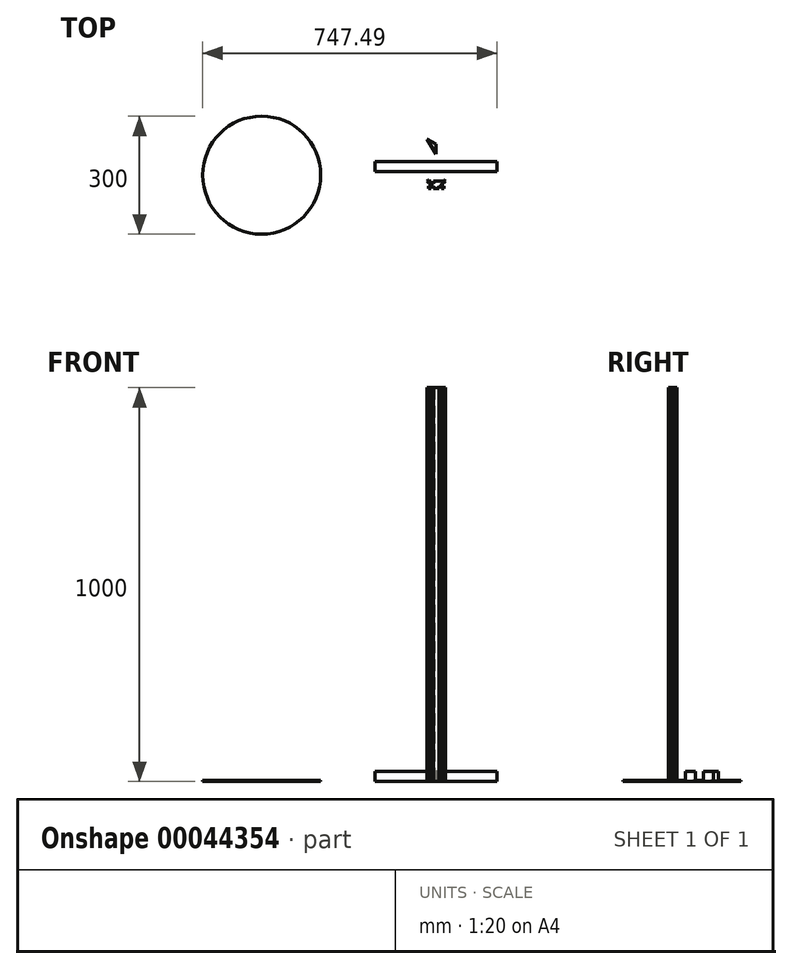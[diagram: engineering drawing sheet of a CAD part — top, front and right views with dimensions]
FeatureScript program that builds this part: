
annotation { "Feature Type Name" : "Feature", "Feature Type Description" : "" }
export const myFeature = defineFeature(function(context is Context, id is Id, definition is map)
    precondition{}
    {
        {
            var Q0;
            Q0=qCreatedBy(makeId("Top.planeOp"),FACE);
            var sketch = newSketch(context, id + "F0", { "sketchPlane" : qUnion([Q0])});
            skCircle(sketch, "E0", {"center": v(-442.49, 24.21) * mm, "radius": 150 * mm});
            skSolve(sketch);
        }
        {
            var Q0;
            Q0=qSketchRegion(id+"F0",true);
            extrude(context, id + "F1", {"entities" : qUnion([Q0]), "depth" : 3 * mm});
        }
        {
            var Q0;
            Q0=qCreatedBy(makeId("Top.planeOp"),FACE);
            var sketch = newSketch(context, id + "F2", { "sketchPlane" : qUnion([Q0])});
            skLineSegment(sketch, "E1", {"start": v(-19.2, 12.03) * mm, "end": v(-20, 12.03) * mm});
            skLineSegment(sketch, "E2", {"start": v(-20, 12.03) * mm, "end": v(-22.38, 9.65) * mm});
            skLineSegment(sketch, "E3", {"start": v(-22.38, 9.65) * mm, "end": v(-20, 7.28) * mm});
            skLineSegment(sketch, "E4", {"start": v(-20, 7.28) * mm, "end": v(-19.2, 7.28) * mm});
            skLineSegment(sketch, "E5", {"start": v(-19.2, 7.28) * mm, "end": v(-19.2, 2.65) * mm});
            skLineSegment(sketch, "E6", {"start": v(-19.2, 2.65) * mm, "end": v(-17.2, 2.65) * mm});
            skLineSegment(sketch, "E7", {"start": v(-17.2, 2.65) * mm, "end": v(-17.2, 5.65) * mm});
            skLineSegment(sketch, "E8", {"start": v(-17.2, 5.65) * mm, "end": v(-16.27, 5.65) * mm});
            skLineSegment(sketch, "E9", {"start": v(-16.27, 5.65) * mm, "end": v(-13.2, 2.6) * mm});
            skLineSegment(sketch, "E10", {"start": v(-13.2, 2.6) * mm, "end": v(-13.2, -3.29) * mm});
            skLineSegment(sketch, "E11", {"start": v(-13.2, -3.29) * mm, "end": v(-16.27, -6.35) * mm});
            skLineSegment(sketch, "E12", {"start": v(-16.27, -6.35) * mm, "end": v(-17.2, -6.35) * mm});
            skLineSegment(sketch, "E13", {"start": v(-17.2, -6.35) * mm, "end": v(-17.2, -3.35) * mm});
            skLineSegment(sketch, "E14", {"start": v(-17.2, -3.35) * mm, "end": v(-19.2, -3.35) * mm});
            skLineSegment(sketch, "E15", {"start": v(-19.2, -3.35) * mm, "end": v(-19.2, -10.35) * mm});
            skLineSegment(sketch, "E16", {"start": v(-19.2, -10.35) * mm, "end": v(-12.2, -10.35) * mm});
            skLineSegment(sketch, "E17", {"start": v(-12.2, -10.35) * mm, "end": v(-12.2, -8.35) * mm});
            skLineSegment(sketch, "E18", {"start": v(-12.2, -8.35) * mm, "end": v(-15.2, -8.35) * mm});
            skLineSegment(sketch, "E19", {"start": v(-15.2, -8.35) * mm, "end": v(-15.2, -7.4) * mm});
            skLineSegment(sketch, "E20", {"start": v(-15.2, -7.4) * mm, "end": v(-12.15, -4.35) * mm});
            skLineSegment(sketch, "E21", {"start": v(-12.15, -4.35) * mm, "end": v(-6.27, -4.35) * mm});
            skLineSegment(sketch, "E22", {"start": v(-6.27, -4.35) * mm, "end": v(-3.2, -7.4) * mm});
            skLineSegment(sketch, "E23", {"start": v(-3.2, -7.4) * mm, "end": v(-3.2, -8.35) * mm});
            skLineSegment(sketch, "E24", {"start": v(-3.2, -8.35) * mm, "end": v(-6.2, -8.35) * mm});
            skLineSegment(sketch, "E25", {"start": v(-6.2, -8.35) * mm, "end": v(-6.2, -10.35) * mm});
            skLineSegment(sketch, "E26", {"start": v(-6.2, -10.35) * mm, "end": v(7.8, -10.35) * mm});
            skLineSegment(sketch, "E27", {"start": v(7.8, -10.35) * mm, "end": v(7.8, -8.35) * mm});
            skLineSegment(sketch, "E28", {"start": v(7.8, -8.35) * mm, "end": v(4.8, -8.35) * mm});
            skLineSegment(sketch, "E29", {"start": v(4.8, -8.35) * mm, "end": v(4.8, -7.4) * mm});
            skLineSegment(sketch, "E30", {"start": v(4.8, -7.4) * mm, "end": v(7.85, -4.35) * mm});
            skLineSegment(sketch, "E31", {"start": v(7.85, -4.35) * mm, "end": v(13.73, -4.35) * mm});
            skLineSegment(sketch, "E32", {"start": v(13.73, -4.35) * mm, "end": v(16.8, -7.4) * mm});
            skLineSegment(sketch, "E33", {"start": v(16.8, -8.35) * mm, "end": v(13.8, -8.35) * mm});
            skLineSegment(sketch, "E34", {"start": v(13.8, -8.35) * mm, "end": v(13.8, -10.35) * mm});
            skLineSegment(sketch, "E35", {"start": v(13.8, -10.35) * mm, "end": v(20.8, -10.35) * mm});
            skLineSegment(sketch, "E36", {"start": v(20.8, -10.35) * mm, "end": v(20.8, -3.35) * mm});
            skLineSegment(sketch, "E37", {"start": v(20.8, -3.35) * mm, "end": v(18.8, -3.35) * mm});
            skLineSegment(sketch, "E38", {"start": v(18.8, -3.35) * mm, "end": v(18.8, -6.35) * mm});
            skLineSegment(sketch, "E39", {"start": v(18.8, -6.35) * mm, "end": v(17.85, -6.35) * mm});
            skLineSegment(sketch, "E40", {"start": v(17.85, -6.35) * mm, "end": v(14.8, -3.29) * mm});
            skLineSegment(sketch, "E41", {"start": v(14.8, -3.29) * mm, "end": v(14.8, 2.6) * mm});
            skLineSegment(sketch, "E42", {"start": v(14.8, 2.6) * mm, "end": v(17.85, 5.65) * mm});
            skLineSegment(sketch, "E43", {"start": v(17.85, 5.65) * mm, "end": v(18.8, 5.65) * mm});
            skLineSegment(sketch, "E44", {"start": v(18.8, 5.65) * mm, "end": v(18.8, 2.65) * mm});
            skLineSegment(sketch, "E45", {"start": v(18.8, 2.65) * mm, "end": v(20.8, 2.65) * mm});
            skLineSegment(sketch, "E46", {"start": v(20.8, 2.65) * mm, "end": v(20.8, 7.28) * mm});
            skLineSegment(sketch, "E47", {"start": v(23.97, 9.65) * mm, "end": v(21.6, 12.03) * mm});
            skLineSegment(sketch, "E48", {"start": v(21.6, 12.03) * mm, "end": v(20.8, 12.03) * mm});
            skLineSegment(sketch, "E49", {"start": v(20.8, 12.03) * mm, "end": v(20.8, 9.65) * mm});
            skLineSegment(sketch, "E50", {"start": v(20.8, 9.65) * mm, "end": v(-6.2, 9.65) * mm});
            skLineSegment(sketch, "E51", {"start": v(-6.2, 9.65) * mm, "end": v(-6.2, 7.65) * mm});
            skLineSegment(sketch, "E52", {"start": v(-6.2, 7.65) * mm, "end": v(-3.2, 7.65) * mm});
            skLineSegment(sketch, "E53", {"start": v(-3.2, 7.65) * mm, "end": v(-3.2, 6.71) * mm});
            skLineSegment(sketch, "E54", {"start": v(-3.2, 6.71) * mm, "end": v(-6.27, 3.65) * mm});
            skLineSegment(sketch, "E55", {"start": v(-6.27, 3.65) * mm, "end": v(-12.15, 3.65) * mm});
            skLineSegment(sketch, "E56", {"start": v(-12.15, 3.65) * mm, "end": v(-15.2, 6.71) * mm});
            skLineSegment(sketch, "E57", {"start": v(-15.2, 6.71) * mm, "end": v(-15.2, 7.65) * mm});
            skLineSegment(sketch, "E58", {"start": v(-15.2, 7.65) * mm, "end": v(-12.2, 7.65) * mm});
            skLineSegment(sketch, "E59", {"start": v(-12.2, 7.65) * mm, "end": v(-12.2, 9.65) * mm});
            skLineSegment(sketch, "E60", {"start": v(-12.2, 9.65) * mm, "end": v(-19.2, 9.65) * mm});
            skLineSegment(sketch, "E61", {"start": v(-19.2, 9.65) * mm, "end": v(-19.2, 12.03) * mm});
            skLineSegment(sketch, "E62", {"start": v(23.97, 9.65) * mm, "end": v(21.6, 7.28) * mm});
            skLineSegment(sketch, "E63", {"start": v(21.6, 7.28) * mm, "end": v(20.8, 7.28) * mm});
            skLineSegment(sketch, "E64", {"start": v(16.8, -7.4) * mm, "end": v(16.8, -8.35) * mm});
            skSolve(sketch);
        }
        {
            var Q0;
            Q0=qSketchRegion(id+"F2",true);
            extrude(context, id + "F3", {"entities" : qUnion([Q0]), "depth" : 1000 * mm});
        }
        {
            var Q0;
            Q0=qCreatedBy(makeId("Right.planeOp"),FACE);
            var sketch = newSketch(context, id + "F4", { "sketchPlane" : qUnion([Q0])});
            skLineSegment(sketch, "E65.bottom", {"start": v(33.21, 0) * mm, "end": v(58.61, 0) * mm});
            skLineSegment(sketch, "E65.top", {"start": v(33.21, 25.4) * mm, "end": v(58.61, 25.4) * mm});
            skLineSegment(sketch, "E65.left", {"start": v(33.21, 0) * mm, "end": v(33.21, 25.4) * mm});
            skLineSegment(sketch, "E65.right", {"start": v(58.61, 0) * mm, "end": v(58.61, 25.4) * mm});
            skSolve(sketch);
        }
        {
            var Q0;
            Q0=qSketchRegion(id+"F4",true);
            extrude(context, id + "F5", {"entities" : qUnion([Q0]), "endBound" : BoundingType.SYMMETRIC, "depth" : 310 * mm});
        }
        {
            var Q0;
            Q0=qCreatedBy(makeId("Top.planeOp"),FACE);
            var sketch = newSketch(context, id + "F6", { "sketchPlane" : qUnion([Q0])});
            skLineSegment(sketch, "E66", {"start": v(0, 78.5) * mm, "end": v(0, 103.9) * mm});
            skLineSegment(sketch, "E67", {"start": v(0, 103.9) * mm, "end": v(-22, 116.6) * mm});
            skLineSegment(sketch, "E68", {"start": v(-22, 116.6) * mm, "end": v(0, 78.5) * mm});
            skSolve(sketch);
        }
        {
            var Q0;
            Q0=qSketchRegion(id+"F6",true);
            extrude(context, id + "F7", {"entities" : qUnion([Q0]), "depth" : 25.4 * mm});
        }
    });
